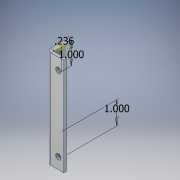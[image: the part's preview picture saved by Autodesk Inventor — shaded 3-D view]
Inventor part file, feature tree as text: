
AUTODESK INVENTOR PART (.ipt)
format: ipt  version: 2017 (Build 210142000, 142)  size: 170,496 bytes
history: native  units: in
note: dims shown in document units (in); Inventor stores cm internally (conversion verified against a paired STEP export)
features: sketch x6, sheet_metal_op x3, hole x2, extrude x1, other x1
ambient origin geometry x8: Origin, YZ Plane, XZ Plane, XY Plane, X Axis, Y Axis, Z Axis, Center Point
bodies: Solid1 (feature_tree)
feature tree (13):
  sketch  "Sketch1"  dims[d0=0.625in d1=4.3in]
  extrude  "Extrusion1"  Depth=4.3in
  sheet_metal_op  "Flange1"
  hole  "Hole1"  [1 undecoded]
  hole  "Hole2"  [1 undecoded]
  sketch  "Sketch6"  dims[d11=0.5in d12=0.125in d13=0.125in d14=0.236in d15=1.0in d16=1.0in d17=0.2362in d18=0.75in d19=0.119in d20=0.25in d21=0.5635in d22=0.125in d23=0.8108in d24=0.236in d25=0.5in d26=0.5in d27=0.2362in d28=0.75in d29=0.119in d30=0.25in d31=0.5635in d32=0.125in d33=0.8108in]
  sketch  "Sketch2"  dims[d2=0.125in d3=0.0in d4=0.125in]
  sketch  "Sketch3"  dims[d5=0.0625in d6=0.25in]
  other  "Plate1"
  sheet_metal_op  "Bend1"
  sheet_metal_op  "Corner1"
  sketch  "Sketch4"  dims[d7=0.125in]
  sketch  "Sketch5"  dims[d8=0.75in d9=90.0deg d10=0.05in]
note: 2 required parameter values undecoded (feature->parameter linkage not recoverable at this tier; creation-order binding heuristic only, values carry confidence <= 0.55)
